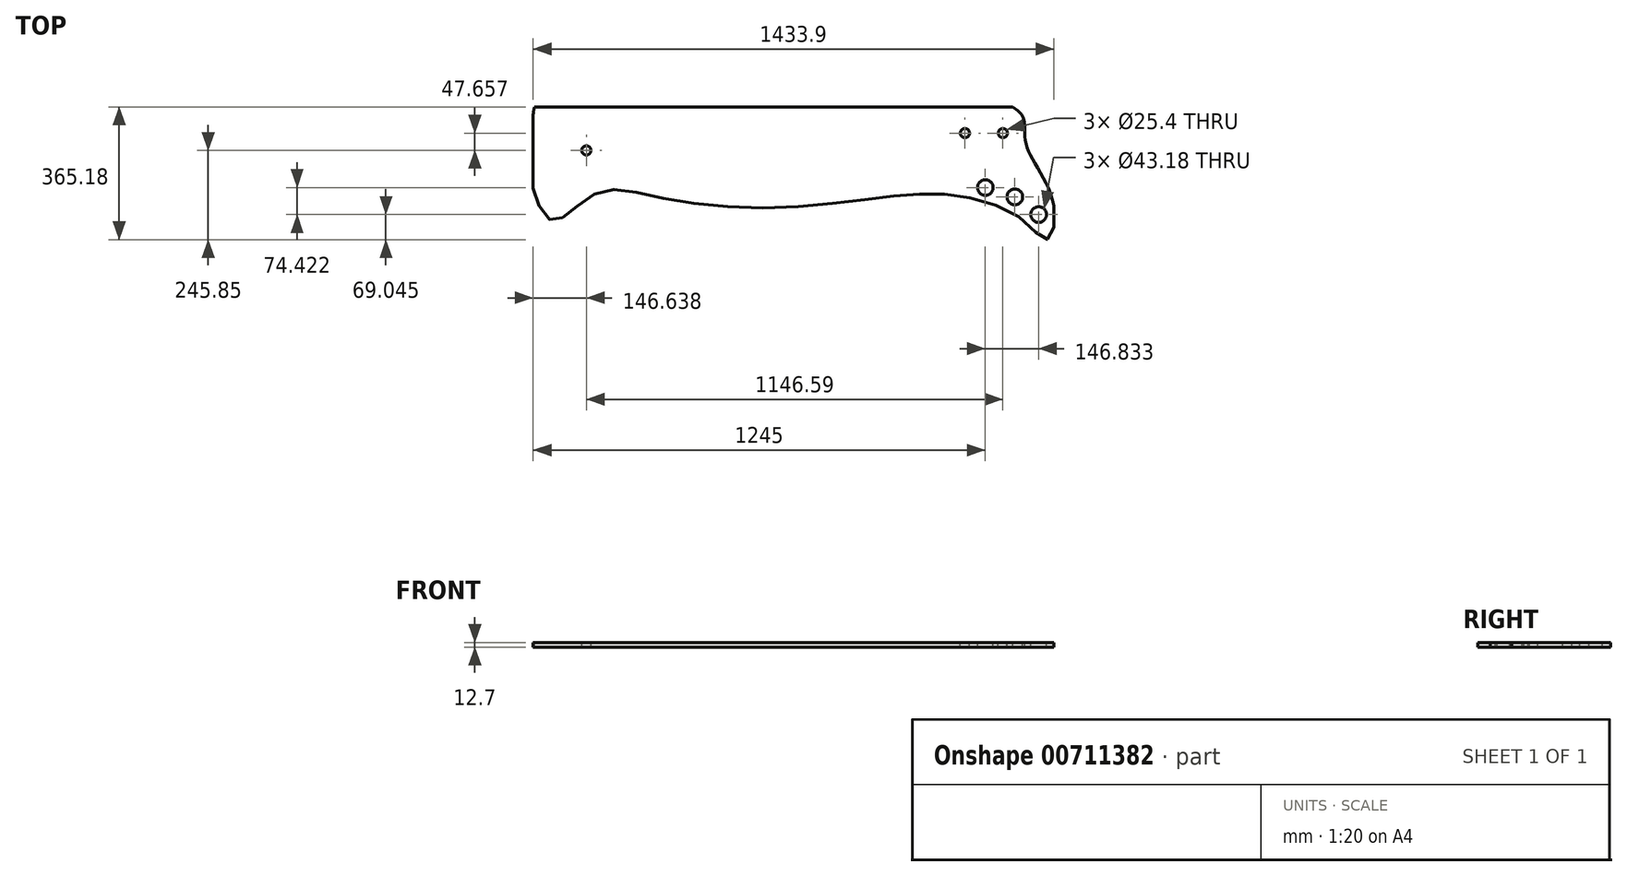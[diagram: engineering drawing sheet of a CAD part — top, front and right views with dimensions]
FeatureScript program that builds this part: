
annotation { "Feature Type Name" : "Feature", "Feature Type Description" : "" }
export const myFeature = defineFeature(function(context is Context, id is Id, definition is map)
    precondition{}
    {
        {
            var Q0;
            Q0=qCreatedBy(makeId("Top.planeOp"),FACE);
            var sketch = newSketch(context, id + "F0", { "sketchPlane" : qUnion([Q0])});
            skLineSegment(sketch, "E0.bottom", {"start": v(19.98, 119.33) * mm, "end": v(1453.88, 119.33) * mm});
            skLineSegment(sketch, "E0.top", {"start": v(19.98, -264.5) * mm, "end": v(1453.88, -264.5) * mm});
            skLineSegment(sketch, "E0.left", {"start": v(19.98, 119.33) * mm, "end": v(19.98, -264.5) * mm});
            skLineSegment(sketch, "E0.right", {"start": v(1453.88, 119.33) * mm, "end": v(1453.88, -264.5) * mm});
            skSolve(sketch);
        }
        {
            var Q0;
            Q0=makeQuery(id+"F0.imprint","IMPRINT",FACE,{"disambiguationData":[TD([[makeQuery(id+"F0.imprint","IMPRINT",EDGE,{"derivedFrom":sQuery(id+"F0.wireOp",EDGE,"E0.bottom")}),-1.0]])]});
            extrude(context, id + "F1", {"entities" : qUnion([Q0]), "depth" : 12.7 * mm, "offsetDistance" : 25.4 * mm});
        }
        {
            var Q0;
            Q0=makeQuery(id+"F1.opExtrude","CAP_FACE",FACE,{"disambiguationData":[OSD([sQuery(id+"F0.wireOp",EDGE,"E0.bottom"),sQuery(id+"F0.wireOp",EDGE,"E0.top"),sQuery(id+"F0.wireOp",EDGE,"E0.left"),sQuery(id+"F0.wireOp",EDGE,"E0.right")])],"isStart":false});
            var sketch = newSketch(context, id + "F2", { "sketchPlane" : qUnion([Q0])});
            skFitSpline(sketch, "E1", {"points": [v(87.44, 164.96) * mm, v(19.98, 96.75) * mm, v(19.98, -12.43) * mm, v(19.98, -72.58) * mm, v(19.98, -103.97) * mm, v(61.55, -187.64) * mm, v(111.35, -177.68) * mm, v(208.96, -111.94) * mm, v(366.34, -129.87) * mm, v(687.07, -157.76) * mm, v(997.84, -127.88) * mm, v(1185.1, -123.9) * mm, v(1368.37, -191.63) * mm, v(1436.1, -245.41) * mm, v(1453.88, -152.78) * mm, v(1391.28, -17.32) * mm, v(1373.35, 48.42) * mm, v(1340.48, 119.33) * mm, v(87.44, 164.96) * mm]});
            skSolve(sketch);
        }
        {
            var Q0;
            {var subQ5=makeQuery(id+"F1.opExtrude","CAP_EDGE",EDGE,{"disambiguationData":[OSD([sQuery(id+"F0.wireOp",EDGE,"E0.top")])],"isStart":false});Q0=makeQuery(id+"F2.imprint","IMPRINT",FACE,{"disambiguationData":[TD([[makeQuery(id+"F2.imprint","IMPRINT",EDGE,{"derivedFrom":subQ5}),1.0]])]});}
            var Q1;
            {var subQ0=sQuery(id+"F2.wireOp",EDGE,"E1");var subQ1=makeQuery(id+"F1.opExtrude","CAP_EDGE",EDGE,{"disambiguationData":[OSD([sQuery(id+"F0.wireOp",EDGE,"E0.left")])],"isStart":false});var subQ2=makeQuery(id+"F2.imprint","INTERSECT",VERTEX,{"disambiguationData":[OD(0.0)],"derivedFrom":[subQ1,subQ0]});Q1=makeQuery(id+"F2.imprint","IMPRINT",FACE,{"disambiguationData":[TD([[makeQuery(id+"F2.imprint","IMPRINT",EDGE,{"disambiguationData":[TD([[subQ2,1.0]])],"derivedFrom":subQ0}),-1.0]])]});}
            var Q2;
            {var subQ0=sQuery(id+"F2.wireOp",EDGE,"E1");var subQ1=makeQuery(id+"F1.opExtrude","CAP_EDGE",EDGE,{"disambiguationData":[OSD([sQuery(id+"F0.wireOp",EDGE,"E0.right")])],"isStart":false});var subQ2=makeQuery(id+"F2.imprint","INTERSECT",VERTEX,{"disambiguationData":[OD(1.0)],"derivedFrom":[subQ1,subQ0]});Q2=makeQuery(id+"F2.imprint","IMPRINT",FACE,{"disambiguationData":[TD([[makeQuery(id+"F2.imprint","IMPRINT",EDGE,{"disambiguationData":[TD([[subQ2,-1.0]])],"derivedFrom":subQ0}),-1.0]])]});}
            extrude(context, id + "F3", {"entities" : qUnion([Q0, Q1, Q2]), "operationType" : NewBodyOperationType.REMOVE, "endBound" : BoundingType.THROUGH_ALL, "oppositeDirection" : true, "depth" : 25.4 * mm, "offsetDistance" : 25.4 * mm});
        }
        {
            var Q0;
            Q0=makeQuery(id+"F1.opExtrude","CAP_FACE",FACE,{"disambiguationData":[OSD([sQuery(id+"F0.wireOp",EDGE,"E0.bottom"),sQuery(id+"F0.wireOp",EDGE,"E0.top"),sQuery(id+"F0.wireOp",EDGE,"E0.left"),sQuery(id+"F0.wireOp",EDGE,"E0.right")])],"isStart":false});
            var sketch = newSketch(context, id + "F4", { "sketchPlane" : qUnion([Q0])});
            skLineSegment(sketch, "E2", {"start": v(121.7, 47.66) * mm, "end": v(1313.2, 47.66) * mm});
            skCircle(sketch, "E3", {"center": v(1313.2, 47.66) * mm, "radius": 12.7 * mm});
            skCircle(sketch, "E4", {"center": v(1208.85, 47.66) * mm, "radius": 12.7 * mm});
            skCircle(sketch, "E5", {"center": v(166.62, 0) * mm, "radius": 12.7 * mm});
            skSolve(sketch);
        }
        {
            var Q0;
            Q0=makeQuery(id+"F4.imprint","IMPRINT",FACE,{"disambiguationData":[TD([[makeQuery(id+"F4.imprint","IMPRINT",EDGE,{"derivedFrom":sQuery(id+"F4.wireOp",EDGE,"E5")}),1.0]])]});
            var Q1;
            {var subQ0=sQuery(id+"F4.wireOp",EDGE,"E4");var subQ1=sQuery(id+"F4.wireOp",EDGE,"E2");var subQ2=makeQuery(id+"F4.imprint","INTERSECT",VERTEX,{"disambiguationData":[OD(0.0)],"derivedFrom":[subQ1,subQ0]});Q1=makeQuery(id+"F4.imprint","IMPRINT",FACE,{"disambiguationData":[TD([[makeQuery(id+"F4.imprint","IMPRINT",EDGE,{"disambiguationData":[TD([[subQ2,-1.0]])],"derivedFrom":subQ1}),-1.0]])]});}
            var Q2;
            {var subQ0=sQuery(id+"F4.wireOp",EDGE,"E4");var subQ1=sQuery(id+"F4.wireOp",EDGE,"E2");var subQ2=makeQuery(id+"F4.imprint","INTERSECT",VERTEX,{"disambiguationData":[OD(0.0)],"derivedFrom":[subQ1,subQ0]});Q2=makeQuery(id+"F4.imprint","IMPRINT",FACE,{"disambiguationData":[TD([[makeQuery(id+"F4.imprint","IMPRINT",EDGE,{"disambiguationData":[TD([[subQ2,-1.0]])],"derivedFrom":subQ1}),1.0]])]});}
            var Q3;
            Q3=makeQuery(id+"F4.imprint","IMPRINT",FACE,{"disambiguationData":[TD([[makeQuery(id+"F4.imprint","IMPRINT",EDGE,{"derivedFrom":sQuery(id+"F4.wireOp",EDGE,"E3")}),1.0]])]});
            extrude(context, id + "F5", {"entities" : qUnion([Q0, Q1, Q2, Q3]), "operationType" : NewBodyOperationType.REMOVE, "oppositeDirection" : true, "depth" : 25.4 * mm, "offsetDistance" : 25.4 * mm});
        }
        {
            var Q0;
            Q0=makeQuery(id+"F1.opExtrude","CAP_FACE",FACE,{"disambiguationData":[OSD([sQuery(id+"F0.wireOp",EDGE,"E0.bottom"),sQuery(id+"F0.wireOp",EDGE,"E0.top"),sQuery(id+"F0.wireOp",EDGE,"E0.left"),sQuery(id+"F0.wireOp",EDGE,"E0.right")])],"isStart":false});
            var sketch = newSketch(context, id + "F6", { "sketchPlane" : qUnion([Q0])});
            skCircle(sketch, "E6", {"center": v(1411.81, -176.8) * mm, "radius": 21.59 * mm});
            skCircle(sketch, "E7", {"center": v(1346.24, -128.13) * mm, "radius": 21.59 * mm});
            skCircle(sketch, "E8", {"center": v(1264.98, -102.38) * mm, "radius": 21.59 * mm});
            skSolve(sketch);
        }
        {
            var Q0;
            Q0 = qSketchRegion(id + "F6", true);
            extrude(context, id + "F7", {"entities" : qUnion([Q0]), "operationType" : NewBodyOperationType.REMOVE, "endBound" : BoundingType.THROUGH_ALL, "oppositeDirection" : true, "depth" : 25.4 * mm, "offsetDistance" : 25.4 * mm});
        }
    });
